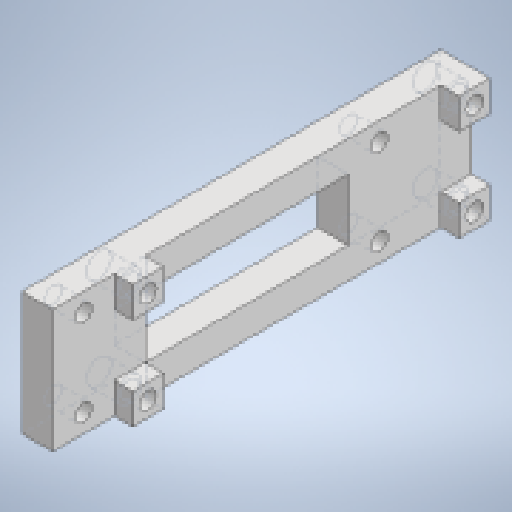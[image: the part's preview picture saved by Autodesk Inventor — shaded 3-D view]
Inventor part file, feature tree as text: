
AUTODESK INVENTOR PART (.ipt)
format: ipt  version: 2023 (Build 270158000, 158)  size: 332,288 bytes
history: native  units: mm
features: extrude x11, sketch x11, projected_geometry x2
ambient origin geometry x8: Origin, YZ Plane, XZ Plane, XY Plane, X Axis, Y Axis, Z Axis, Center Point
bodies: Solid1 (feature_tree)
feature tree (24):
  extrude  "Extrusion1"  Depth=5.0mm
  extrude  "Extrusion2"  Depth=15.0mm
  extrude  "Extrusion3"  Depth=48.0mm
  extrude  "Extrusion4"  Depth=10.0mm
  extrude  "Extrusion5"  Depth=10.0mm
  extrude  "Extrusion6"  Depth=5.0mm TaperAngle=0.0deg
  extrude  "Extrusion7"  Depth=5.0mm
  extrude  "Extrusion8"  Depth=10.0mm
  extrude  "Extrusion9"  Depth=3.0mm
  extrude  "Extrusion10"  Depth=5.0mm
  extrude  "Extrusion11"  Depth=5.0mm
  sketch  "Sketch1"  dims[d0=5.0mm d1=5.0mm]
  sketch  "Sketch2"  dims[d2=5.0mm d3=15.0mm]
  sketch  "Sketch3"  dims[d4=15.0mm d5=48.0mm]
  sketch  "Sketch4"  dims[d6=20.0mm d7=0.0mm d8=10.0mm]
  sketch  "Sketch5"  dims[d9=10.0mm d10=10.0mm]
  sketch  "Sketch6"  dims[d11=5.0mm d12=200.0mm d13=0.0mm]
  sketch  "Sketch7"  dims[d14=5.0mm d15=5.0mm]
  projected_geometry  "Projected Loop1"
  sketch  "Sketch8"  dims[d16=20.0mm d17=0.0mm d18=10.0mm]
  projected_geometry  "Projected Loop2"
  sketch  "Sketch9"  dims[d19=10.0mm d20=3.0mm]
  sketch  "Sketch10"  dims[d21=3.0mm d22=5.0mm]
  sketch  "Sketch11"  dims[d23=5.0mm d24=5.0mm d25=5.0mm d26=3.0mm d27=3.0mm d28=2.75mm d29=2.75mm d30=2.75mm d31=2.75mm d32=5.0mm d33=0.0mm d34=2.5mm d35=2.5mm d36=2.5mm d37=2.5mm d38=2.5mm d39=2.5mm d40=2.5mm d41=2.5mm d42=2.75mm d43=2.75mm d44=2.75mm d45=2.75mm d46=15.0mm d47=0.0mm d48=4.0mm d49=4.0mm d50=4.0mm d51=4.0mm d52=3.0mm d53=0.0mm d54=12.0mm d55=4.0mm d56=3.0mm d57=5.0mm d58=5.0mm d59=3.0mm d60=3.0mm d61=1000.0mm d62=0.0mm d63=0.0mm d64=0.0mm d65=10.0mm d66=5.0mm d67=0.0mm d68=5.0mm d69=3.0mm d70=3.0mm d71=3.0mm d72=5.0mm d73=5.0mm d74=2.75mm d75=2.75mm d76=2.75mm d77=5.0mm d78=0.0mm d79=5.0mm d80=5.0mm d81=0.0mm d82=4.0mm d83=4.0mm d84=4.0mm d85=4.0mm d86=2.0mm d87=0.0mm]
